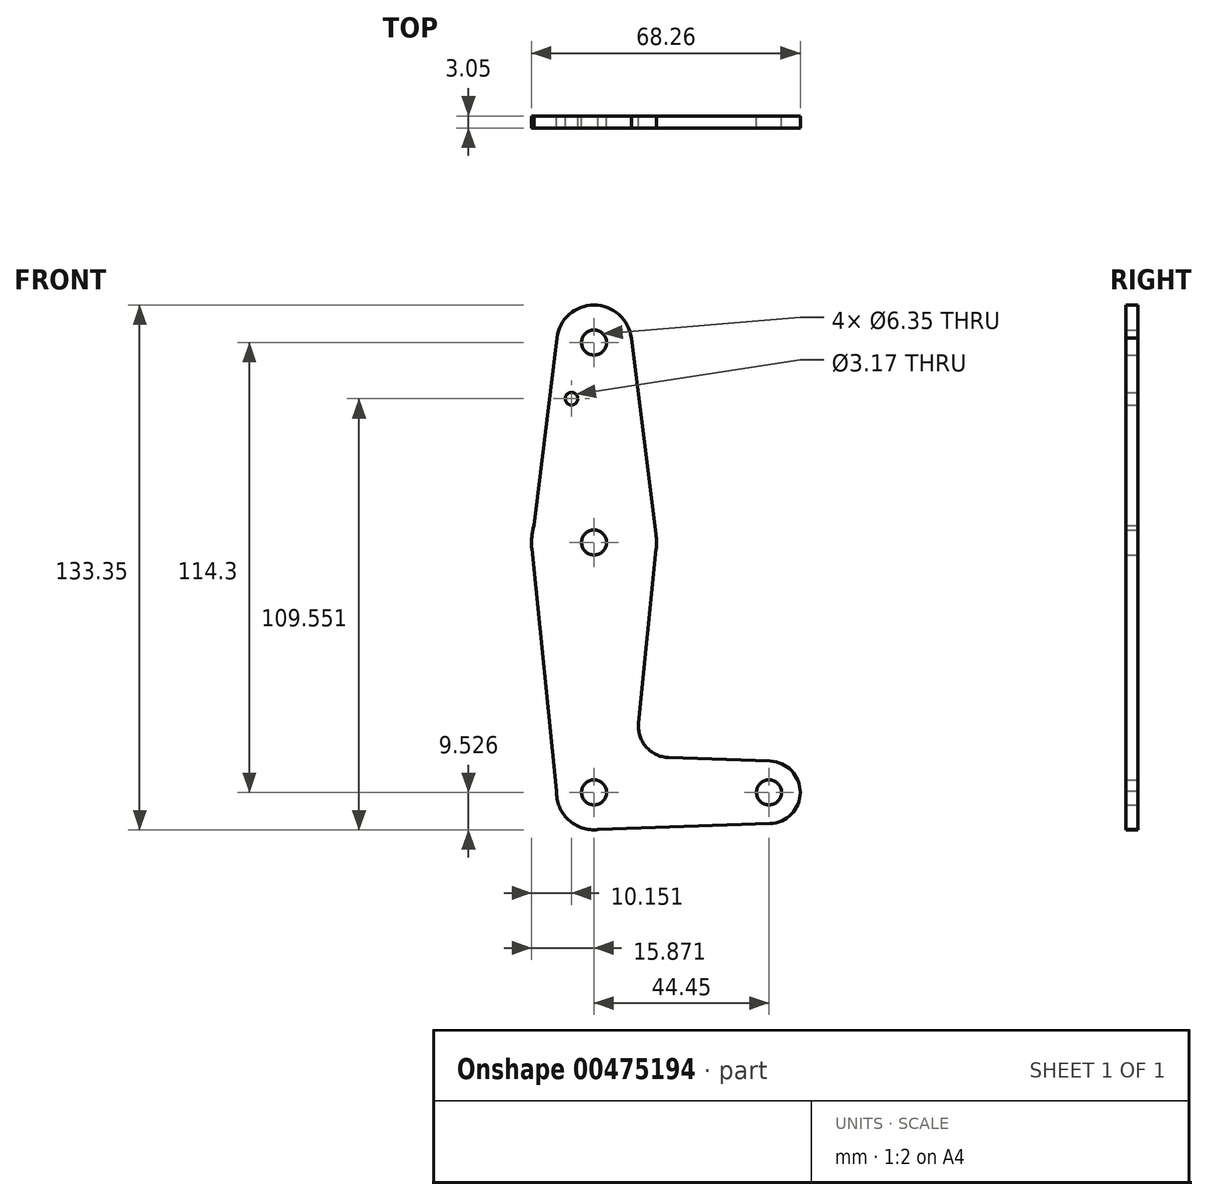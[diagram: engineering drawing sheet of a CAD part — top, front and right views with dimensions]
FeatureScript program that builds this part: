
annotation { "Feature Type Name" : "Feature", "Feature Type Description" : "" }
export const myFeature = defineFeature(function(context is Context, id is Id, definition is map)
    precondition{}
    {
        {
            var Q0;
            Q0=qCreatedBy(makeId("Front.planeOp"),FACE);
            var sketch = newSketch(context, id + "F0", { "sketchPlane" : qUnion([Q0])});
            skLineSegment(sketch, "E0", {"start": v(-55.36, 58.98) * mm, "end": v(-55.36, -55.32) * mm});
            skLineSegment(sketch, "E1", {"start": v(-55.36, -55.32) * mm, "end": v(-10.9, -55.32) * mm});
            skCircle(sketch, "E2", {"center": v(-55.36, 58.98) * mm, "radius": 9.53 * mm});
            skCircle(sketch, "E3", {"center": v(-55.36, -55.32) * mm, "radius": 9.53 * mm});
            skCircle(sketch, "E4", {"center": v(-10.9, -55.32) * mm, "radius": 7.94 * mm});
            skCircle(sketch, "E5", {"center": v(-55.36, 8.18) * mm, "radius": 15.88 * mm});
            skCircle(sketch, "E6", {"center": v(-55.36, 58.98) * mm, "radius": 3.18 * mm});
            skCircle(sketch, "E7", {"center": v(-55.36, 8.18) * mm, "radius": 3.18 * mm});
            skCircle(sketch, "E8", {"center": v(-55.36, -55.32) * mm, "radius": 3.18 * mm});
            skCircle(sketch, "E9", {"center": v(-10.9, -55.32) * mm, "radius": 3.18 * mm});
            skCircle(sketch, "E10", {"center": v(-61.08, 44.7) * mm, "radius": 1.59 * mm});
            skLineSegment(sketch, "E11", {"start": v(-36.42, -46.47) * mm, "end": v(-10.63, -47.4) * mm});
            skLineSegment(sketch, "E12", {"start": v(-55.7, -64.84) * mm, "end": v(-10.63, -63.26) * mm});
            skLineSegment(sketch, "E13", {"start": v(-64.88, -54.96) * mm, "end": v(-71.15, 6.57) * mm});
            skLineSegment(sketch, "E14", {"start": v(-44.05, -37.73) * mm, "end": v(-39.56, 6.58) * mm});
            skLineSegment(sketch, "E15", {"start": v(-64.81, 60.13) * mm, "end": v(-70.64, 12.48) * mm});
            skLineSegment(sketch, "E16", {"start": v(-45.9, 60.07) * mm, "end": v(-39.6, 10.16) * mm});
            skArc(sketch, "E17.filletArc", {"start": v(-44.05, -37.73) * mm, "mid": v(-42.13, -43.75) * mm, "end": v(-36.42, -46.47) * mm});
            skSolve(sketch);
        }
        {
            var Q0;
            Q0 = qSketchRegion(id + "F0", true);
            var Q1;
            {var subQ0=sQuery(id+"F0.wireOp",EDGE,"E3");var subQ1=sQuery(id+"F0.wireOp",EDGE,"E0");var subQ2=makeQuery(id+"F0.imprint","INTERSECT",VERTEX,{"derivedFrom":[subQ1,subQ0]});Q1=makeQuery(id+"F0.imprint","IMPRINT",FACE,{"disambiguationData":[TD([[makeQuery(id+"F0.imprint","IMPRINT",EDGE,{"disambiguationData":[TD([[subQ2,-1.0]])],"derivedFrom":subQ1}),1.0]])]});}
            extrude(context, id + "F1", {"entities" : qUnion([Q0, Q1]), "depth" : 3.05 * mm});
        }
    });
